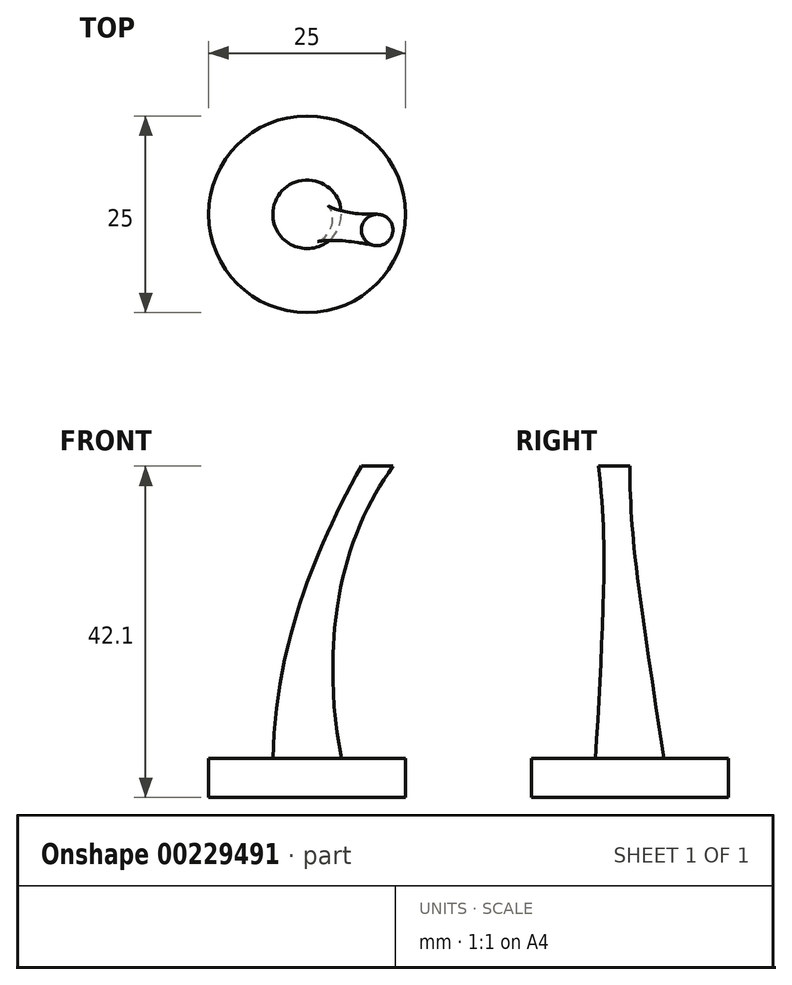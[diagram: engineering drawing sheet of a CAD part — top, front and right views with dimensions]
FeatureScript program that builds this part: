
annotation { "Feature Type Name" : "Feature", "Feature Type Description" : "" }
export const myFeature = defineFeature(function(context is Context, id is Id, definition is map)
    precondition{}
    {
        {
            var Q0;
            Q0=qCreatedBy(makeId("Top.planeOp"),FACE);
            var sketch = newSketch(context, id + "F0", { "sketchPlane" : qUnion([Q0])});
            skCircle(sketch, "E0", {"center": v(0, 0) * mm, "radius": 12.5 * mm});
            skSolve(sketch);
        }
        {
            var Q0;
            Q0=makeQuery(id+"F0.imprint","IMPRINT",FACE,{"disambiguationData":[TD([[makeQuery(id+"F0.imprint","IMPRINT",EDGE,{"derivedFrom":sQuery(id+"F0.wireOp",EDGE,"E0")}),1.0]])]});
            extrude(context, id + "F1", {"entities" : qUnion([Q0]), "depth" : 5 * mm});
        }
        {
            var Q0;
            Q0=qCreatedBy(makeId("Front.planeOp"),FACE);
            var sketch = newSketch(context, id + "F2", { "sketchPlane" : qUnion([Q0])});
            skArc(sketch, "E1", {"start": v(8.9, 42.1) * mm, "mid": v(-0.7, 24.61) * mm, "end": v(-4.35, 5) * mm});
            skSolve(sketch);
        }
        {
            var Q0;
            Q0=sQuery(id+"F2.wireOp",VERTEX,"E1.start");
            var Q1;
            Q1=qCreatedBy(makeId("Top.planeOp"),FACE);
            cPlane(context, id + "F3", {"entities" : qUnion([Q0, Q1]), "cplaneType" : CPlaneType.PLANE_POINT, "offset" : 25 * mm, "width" : 150 * mm, "height" : 150 * mm});
        }
        {
            var Q0;
            Q0=qCreatedBy(id+"F3.planeOp",FACE);
            var sketch = newSketch(context, id + "F4", { "sketchPlane" : qUnion([Q0])});
            skCircle(sketch, "E2", {"center": v(8.9, -2) * mm, "radius": 2 * mm});
            skSolve(sketch);
        }
        {
            var Q0;
            Q0=makeQuery(id+"F1.opExtrude","CAP_FACE",FACE,{"disambiguationData":[OSD([sQuery(id+"F0.wireOp",EDGE,"E0")])],"isStart":false});
            var sketch = newSketch(context, id + "F5", { "sketchPlane" : qUnion([Q0])});
            skCircle(sketch, "E3", {"center": v(0, 0) * mm, "radius": 4.35 * mm});
            skSolve(sketch);
        }
        {
            var Q0;
            Q0=makeQuery(id+"F5.imprint","IMPRINT",FACE,{"disambiguationData":[TD([[makeQuery(id+"F5.imprint","IMPRINT",EDGE,{"derivedFrom":sQuery(id+"F5.wireOp",EDGE,"E3")}),1.0]])]});
            var Q1;
            Q1=makeQuery(id+"F4.imprint","IMPRINT",FACE,{"disambiguationData":[TD([[makeQuery(id+"F4.imprint","IMPRINT",EDGE,{"derivedFrom":sQuery(id+"F4.wireOp",EDGE,"E2")}),1.0]])]});
            var Q2;
            Q2=sQuery(id+"F2.wireOp",EDGE,"E1");
            loft(context, id + "F6", {"operationType" : NewBodyOperationType.ADD, "addGuides" : true, "sheetProfilesArray" : [{ "sheetProfileEntities" : qUnion([Q0]) }, { "sheetProfileEntities" : qUnion([Q1]) }], "guidesArray" : [{ "guideEntities" : qUnion([Q2]), "guideDerivativeType" : LoftGuideDerivativeType.DEFAULT, "guideDerivativeMagnitude" : 1 }]});
        }
    });
